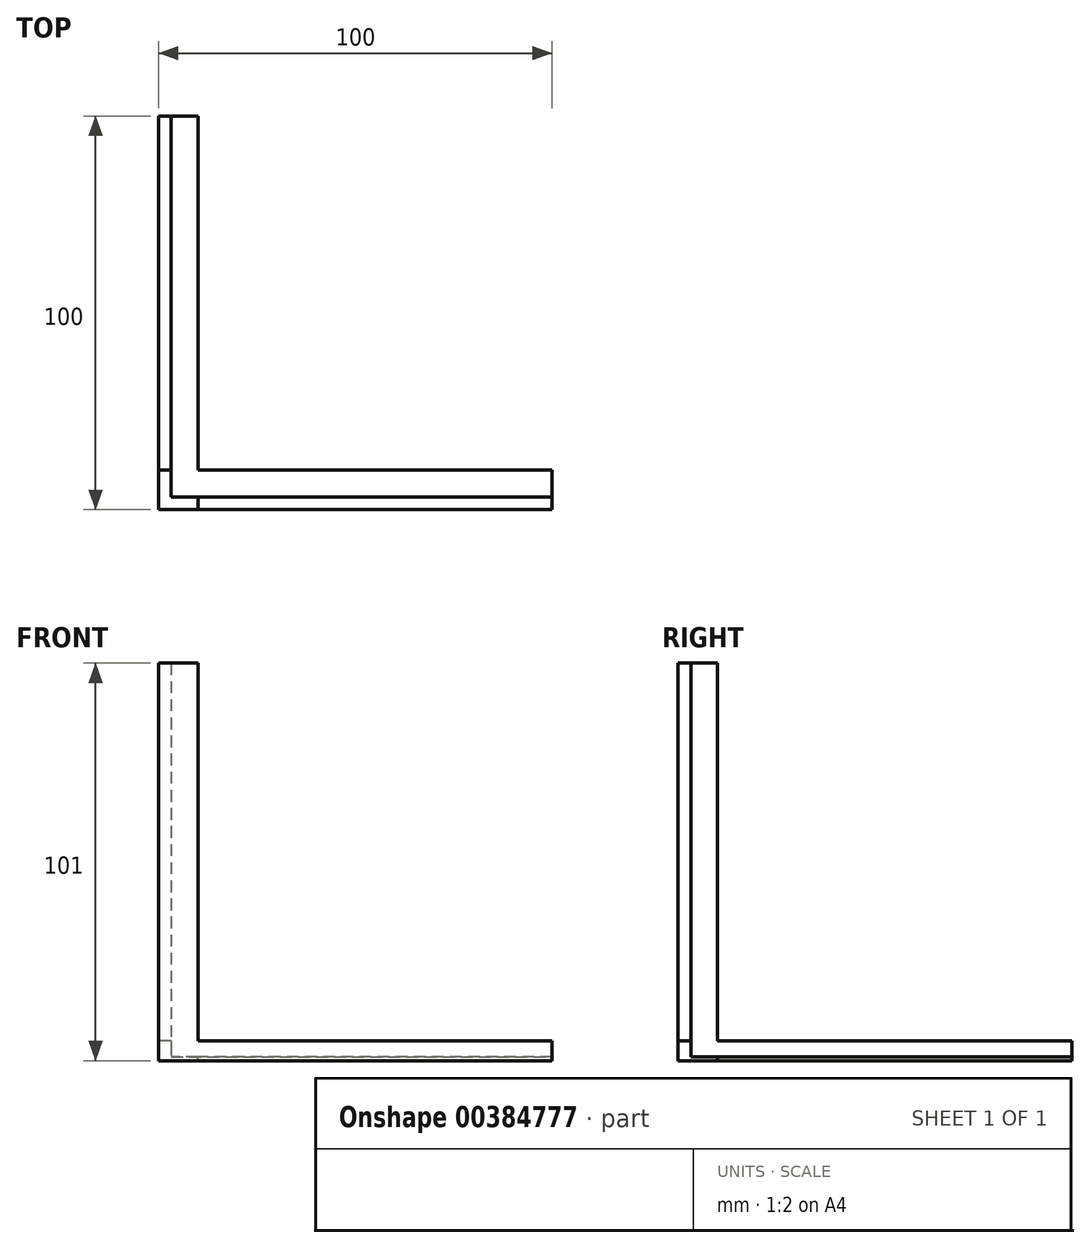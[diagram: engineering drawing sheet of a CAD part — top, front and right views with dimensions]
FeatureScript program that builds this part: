
annotation { "Feature Type Name" : "Feature", "Feature Type Description" : "" }
export const myFeature = defineFeature(function(context is Context, id is Id, definition is map)
    precondition{}
    {
        {
            var Q0;
            Q0=qCreatedBy(makeId("Top.planeOp"),FACE);
            var sketch = newSketch(context, id + "F0", { "sketchPlane" : qUnion([Q0])});
            skLineSegment(sketch, "E0", {"start": v(-36.06, 58.8) * mm, "end": v(-36.06, -41.2) * mm});
            skLineSegment(sketch, "E1", {"start": v(-36.06, -41.2) * mm, "end": v(63.94, -41.2) * mm});
            skLineSegment(sketch, "E2", {"start": v(63.94, -41.2) * mm, "end": v(63.94, -31.2) * mm});
            skLineSegment(sketch, "E3", {"start": v(63.94, -31.2) * mm, "end": v(-26.06, -31.2) * mm});
            skLineSegment(sketch, "E4", {"start": v(-26.06, -31.2) * mm, "end": v(-26.06, 58.8) * mm});
            skLineSegment(sketch, "E5", {"start": v(-26.06, 58.8) * mm, "end": v(-36.06, 58.8) * mm});
            skLineSegment(sketch, "E6", {"start": v(-32.86, 58.8) * mm, "end": v(-32.86, -38) * mm});
            skLineSegment(sketch, "E7", {"start": v(-32.86, -38) * mm, "end": v(63.94, -38) * mm});
            skLineSegment(sketch, "E8", {"start": v(-36.06, -31.2) * mm, "end": v(-32.86, -31.2) * mm});
            skLineSegment(sketch, "E9", {"start": v(-32.86, -31.2) * mm, "end": v(-26.06, -38) * mm});
            skLineSegment(sketch, "E10", {"start": v(-26.06, -38) * mm, "end": v(-26.06, -41.2) * mm});
            skSolve(sketch);
        }
        {
            var Q0;
            Q0 = qSketchRegion(id + "F0", true);
            var Q1;
            {var subQ3=sQuery(id+"F0.wireOp",EDGE,"E9");Q1=makeQuery(id+"F0.imprint","IMPRINT",FACE,{"disambiguationData":[TD([[makeQuery(id+"F0.imprint","IMPRINT",EDGE,{"derivedFrom":subQ3}),-1.0]])]});}
            extrude(context, id + "F1", {"entities" : qUnion([Q0, Q1]), "oppositeDirection" : true, "depth" : 1 * mm});
        }
        {
            var Q0;
            {var subQ3=sQuery(id+"F0.wireOp",EDGE,"E8");Q0=makeQuery(id+"F0.imprint","IMPRINT",FACE,{"disambiguationData":[TD([[makeQuery(id+"F0.imprint","IMPRINT",EDGE,{"derivedFrom":subQ3}),1.0]])]});}
            var Q1;
            {var subQ8=sQuery(id+"F0.wireOp",EDGE,"E8");Q1=makeQuery(id+"F0.imprint","IMPRINT",FACE,{"disambiguationData":[TD([[makeQuery(id+"F0.imprint","IMPRINT",EDGE,{"derivedFrom":subQ8}),-1.0]])]});}
            var Q2;
            {var subQ3=sQuery(id+"F0.wireOp",EDGE,"E10");Q2=makeQuery(id+"F0.imprint","IMPRINT",FACE,{"disambiguationData":[TD([[makeQuery(id+"F0.imprint","IMPRINT",EDGE,{"derivedFrom":subQ3}),1.0]])]});}
            extrude(context, id + "F2", {"entities" : qUnion([Q0, Q1, Q2]), "operationType" : NewBodyOperationType.ADD, "depth" : 4 * mm});
        }
        {
            var Q0;
            {var subQ8=sQuery(id+"F0.wireOp",EDGE,"E8");Q0=makeQuery(id+"F0.imprint","IMPRINT",FACE,{"disambiguationData":[TD([[makeQuery(id+"F0.imprint","IMPRINT",EDGE,{"derivedFrom":subQ8}),-1.0]])]});}
            extrude(context, id + "F3", {"entities" : qUnion([Q0]), "operationType" : NewBodyOperationType.ADD, "depth" : 100 * mm});
        }
    });
